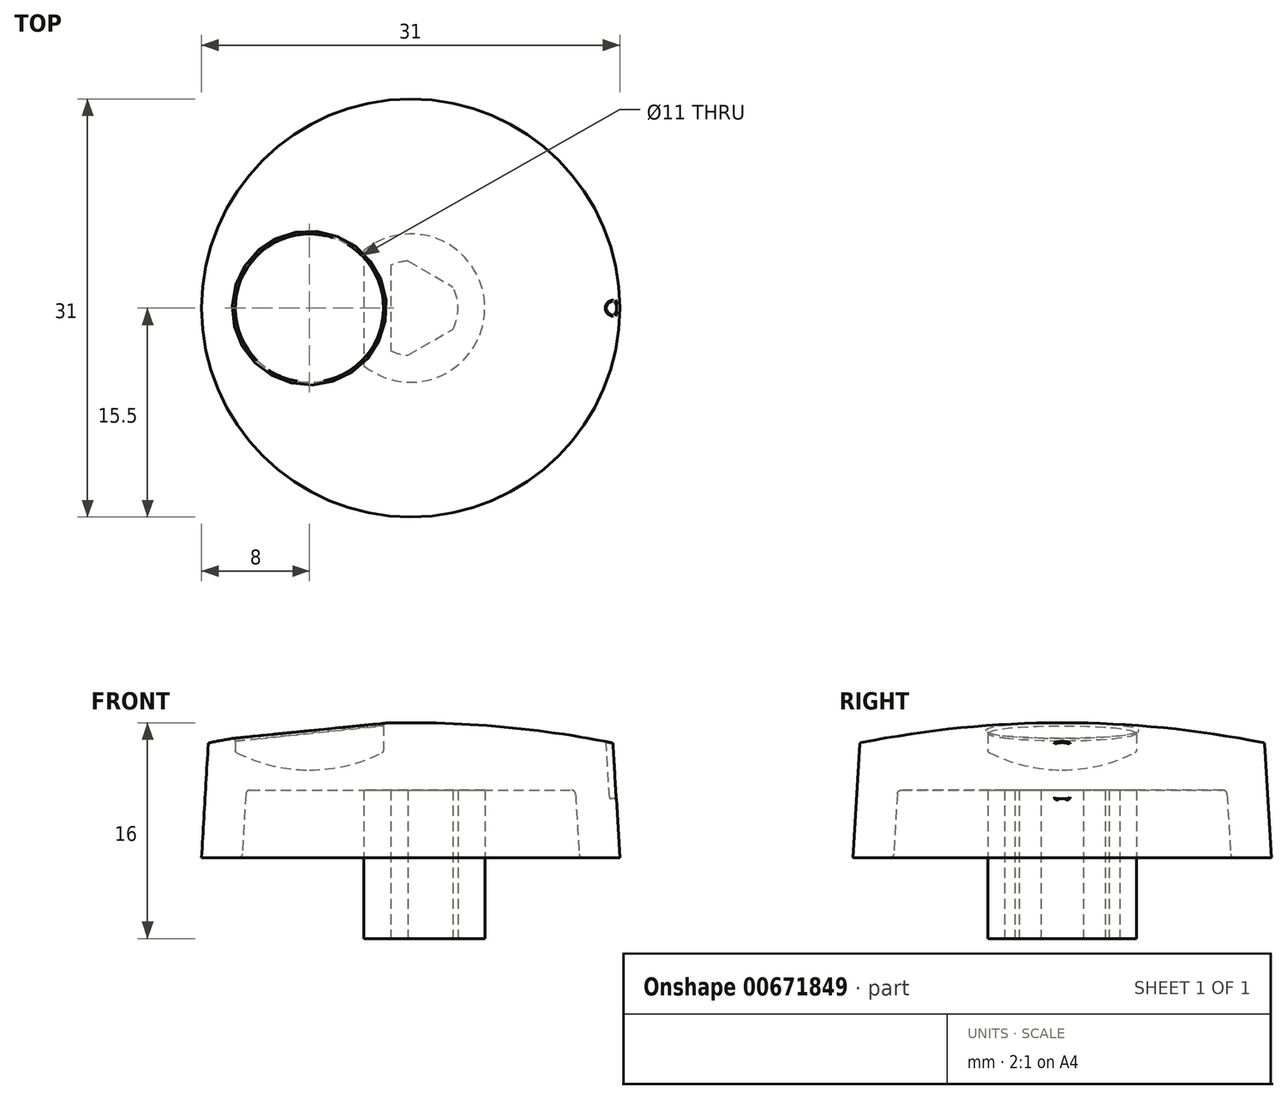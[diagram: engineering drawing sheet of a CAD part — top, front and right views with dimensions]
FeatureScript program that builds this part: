
annotation { "Feature Type Name" : "Feature", "Feature Type Description" : "" }
export const myFeature = defineFeature(function(context is Context, id is Id, definition is map)
    precondition{}
    {
        {
            assignVariable(context, id + "F0", {"name" : "height_above_panel", "anyValue" : 11});
        }
        {
            assignVariable(context, id + "F1", {"name" : "grip_depth_factor", "anyValue" : 0.75});
        }
        {
            var Q0;
            Q0=qCreatedBy(makeId("Top.planeOp"),FACE);
            var sketch = newSketch(context, id + "F2", { "sketchPlane" : qUnion([Q0])});
            skArc(sketch, "E0", {"start": v(-3.46, -4.27) * mm, "mid": v(5.5, 0) * mm, "end": v(-3.46, 4.27) * mm});
            skArc(sketch, "E1", {"start": v(-1.46, -2.62) * mm, "mid": v(3, 0.02) * mm, "end": v(-1.5, 2.6) * mm, "construction": true});
            skCircle(sketch, "E2", {"center": v(0, 0) * mm, "radius": 15.5 * mm, "construction": true});
            skLineSegment(sketch, "E3", {"start": v(-1.46, 3.18) * mm, "end": v(-1.46, -3.18) * mm});
            skLineSegment(sketch, "E4", {"start": v(-3.46, 4.27) * mm, "end": v(-3.46, -4.27) * mm});
            skArc(sketch, "E5", {"start": v(-1.46, -3.18) * mm, "mid": v(-0.85, -3.4) * mm, "end": v(-0.2, -3.5) * mm});
            skLineSegment(sketch, "E6", {"start": v(-0.2, -3.5) * mm, "end": v(3.13, -1.57) * mm});
            skArc(sketch, "E7.trimOffspring", {"start": v(3.13, -1.57) * mm, "mid": v(3.5, 0) * mm, "end": v(3.13, 1.57) * mm});
            skArc(sketch, "E8.trimOffspring", {"start": v(-0.2, 3.5) * mm, "mid": v(-0.85, 3.4) * mm, "end": v(-1.46, 3.18) * mm});
            skLineSegment(sketch, "E9.trimOffspring", {"start": v(-0.2, 3.5) * mm, "end": v(3.13, 1.57) * mm});
            skArc(sketch, "E10.0", {"start": v(-1.5, -2.51) * mm, "mid": v(2.92, -0.02) * mm, "end": v(-1.46, 2.53) * mm, "construction": true});
            skLineSegment(sketch, "E11", {"start": v(-1.5, 2.6) * mm, "end": v(-1.5, -2.51) * mm, "construction": true});
            skSolve(sketch);
        }
        {
            var Q0;
            Q0=qSketchRegion(id+"F2",true);
            extrude(context, id + "F3", {"entities" : qUnion([Q0]), "depth" : 11 * mm});
        }
        {
            var Q0;
            Q0=qCreatedBy(makeId("Top.planeOp"),FACE);
            cPlane(context, id + "F4", {"entities" : qUnion([Q0]), "cplaneType" : CPlaneType.OFFSET, "offset" : 5 * mm, "width" : 150 * mm, "height" : 150 * mm});
        }
        {
            var Q0;
            Q0=qCreatedBy(makeId("Front.planeOp"),FACE);
            var sketch = newSketch(context, id + "F5", { "sketchPlane" : qUnion([Q0])});
            skLineSegment(sketch, "E12.0", {"start": v(-3.46, 11) * mm, "end": v(5.5, 11) * mm});
            skLineSegment(sketch, "E13", {"start": v(0, 11) * mm, "end": v(0, 16) * mm});
            skArc(sketch, "E14", {"start": v(15, 14.5) * mm, "mid": v(7.54, 15.62) * mm, "end": v(0, 16) * mm});
            skLineSegment(sketch, "E15", {"start": v(-10.14, 16) * mm, "end": v(12.68, 16) * mm, "construction": true});
            skLineSegment(sketch, "E16", {"start": v(15, 14.5) * mm, "end": v(15.5, 6) * mm});
            skLineSegment(sketch, "E17", {"start": v(15.5, 6) * mm, "end": v(12.5, 6) * mm});
            skLineSegment(sketch, "E18", {"start": v(12.5, 6) * mm, "end": v(12.2, 11) * mm});
            skLineSegment(sketch, "E19", {"start": v(5.5, 11) * mm, "end": v(12.2, 11) * mm});
            skSolve(sketch);
        }
        {
            var Q0;
            {var subQ0=sQuery(id+"F5.wireOp",EDGE,"E13");Q0=makeQuery(id+"F5.imprint","IMPRINT",FACE,{"disambiguationData":[TD([[makeQuery(id+"F5.imprint","IMPRINT",EDGE,{"derivedFrom":subQ0}),-1.0]])]});}
            var Q1;
            Q1=sQuery(id+"F5.wireOp",EDGE,"E13");
            revolve(context, id + "F6", {"operationType" : NewBodyOperationType.ADD, "entities" : qUnion([Q0]), "axis" : qUnion([Q1]), "revolveType" : RevolveType.FULL});
        }
        {
            var Q0;
            Q0=qCreatedBy(makeId("Front.planeOp"),FACE);
            var sketch = newSketch(context, id + "F7", { "sketchPlane" : qUnion([Q0])});
            skLineSegment(sketch, "E20.0", {"start": v(15, 14.5) * mm, "end": v(-15, 14.5) * mm});
            skLineSegment(sketch, "E21.bottom", {"start": v(-13, 24.51) * mm, "end": v(-7.5, 24.51) * mm});
            skLineSegment(sketch, "E21.top", {"start": v(-13, 13.83) * mm, "end": v(-7.5, 13.83) * mm});
            skLineSegment(sketch, "E21.left", {"start": v(-13, 24.51) * mm, "end": v(-13, 13.83) * mm});
            skLineSegment(sketch, "E21.right", {"start": v(-7.5, 24.51) * mm, "end": v(-7.5, 13.83) * mm});
            skLineSegment(sketch, "E22", {"start": v(-15.04, 12.5) * mm, "end": v(-4.86, 12.5) * mm, "construction": true});
            skArc(sketch, "E23", {"start": v(-13, 13.83) * mm, "mid": v(-10.33, 12.84) * mm, "end": v(-7.5, 12.5) * mm});
            skLineSegment(sketch, "E24", {"start": v(-7.5, 13.83) * mm, "end": v(-7.5, 12.5) * mm});
            skSolve(sketch);
        }
        {
            var Q0;
            Q0=qSketchRegion(id+"F7",true);
            var Q1;
            Q1=sQuery(id+"F7.wireOp",EDGE,"E21.right");
            revolve(context, id + "F8", {"operationType" : NewBodyOperationType.REMOVE, "entities" : qUnion([Q0]), "axis" : qUnion([Q1]), "revolveType" : RevolveType.FULL, "oppositeDirection" : true});
        }
        {
            var Q0;
            Q0=sQuery(id+"F5.wireOp",EDGE,"E16");
            var Q1;
            Q1=sQuery(id+"F5.wireOp",VERTEX,"E16.start");
            cPlane(context, id + "F9", {"entities" : qUnion([Q0, Q1]), "cplaneType" : CPlaneType.LINE_POINT, "offset" : 25 * mm, "width" : 150 * mm, "height" : 150 * mm});
        }
        {
            var Q0;
            Q0=qCreatedBy(id+"F9.planeOp",FACE);
            var sketch = newSketch(context, id + "F10", { "sketchPlane" : qUnion([Q0])});
            skPoint(sketch, "E25.0", {"position": v(15.83, 0) * mm});
            skCircle(sketch, "E26", {"center": v(15.83, 0) * mm, "radius": 0.5 * mm});
            skSolve(sketch);
        }
        {
            var Q0;
            Q0=makeQuery(id+"F10.imprint","IMPRINT",FACE,{"disambiguationData":[TD([[makeQuery(id+"F10.imprint","IMPRINT",EDGE,{"derivedFrom":sQuery(id+"F10.wireOp",EDGE,"E26")}),1.0]])]});
            extrude(context, id + "F11", {"entities" : qUnion([Q0]), "operationType" : NewBodyOperationType.REMOVE, "endBound" : BoundingType.SYMMETRIC, "depth" : (getVariable(context, 'grip_depth_factor') * getVariable(context, 'height_above_panel')) * mm});
        }
        {
            var Q0;
            Q0=makeQuery(id+"F11.boolean.opBoolean","COPY",FACE,{"derivedFrom":makeQuery(id+"F11.opExtrude","SWEPT_FACE",FACE,{"disambiguationData":[OSD([sQuery(id+"F10.wireOp",EDGE,"E26")])]})});
            var Q1;
            Q1=makeQuery(id+"F6.opRevolve","SWEPT_EDGE",EDGE,{"disambiguationData":[OSD([sQuery(id+"F5.wireOp",EDGE,"E14"),sQuery(id+"F5.wireOp",EDGE,"E16")])]});
            fillet(context, id + "F12", {"entities" : qUnion([Q0, Q1]), "radius" : 0.1 * mm, "tangentPropagation" : true, "allowEdgeOverflow" : false});
        }
        {
            var Q0;
            Q0=makeQuery(id+"F8.boolean.opBoolean","INTERSECT",EDGE,{"derivedFrom":[makeQuery(id+"F6.opRevolve","SWEPT_FACE",FACE,{"disambiguationData":[OSD([sQuery(id+"F5.wireOp",EDGE,"E14")])]}),makeQuery(id+"F8.opRevolve","SWEPT_FACE",FACE,{"disambiguationData":[OSD([sQuery(id+"F7.wireOp",EDGE,"E21.left")])]})]});
            var Q1;
            Q1=makeQuery(id+"F8.boolean.opBoolean","COPY",EDGE,{"derivedFrom":makeQuery(id+"F8.opRevolve","SWEPT_EDGE",EDGE,{"disambiguationData":[OSD([sQuery(id+"F7.wireOp",EDGE,"E21.top"),sQuery(id+"F7.wireOp",EDGE,"E21.left"),sQuery(id+"F7.wireOp",EDGE,"E23")])]})});
            fillet(context, id + "F13", {"entities" : qUnion([Q0, Q1]), "radius" : 0.2 * mm, "tangentPropagation" : true, "allowEdgeOverflow" : false});
        }
        {
            var Q0;
            Q0=makeQuery(id+"F6.opRevolve","SWEPT_EDGE",EDGE,{"disambiguationData":[OSD([sQuery(id+"F5.wireOp",EDGE,"E18"),sQuery(id+"F5.wireOp",EDGE,"EPLxxkZY-Jm2v-z4IR-q4Ga-VjId1qaTgEh2")])]});
            var Q1;
            Q1=makeQuery(id+"F6.boolean.opBoolean","MERGE",EDGE,{"derivedFrom":[makeQuery(id+"F3.opExtrude","CAP_EDGE",EDGE,{"disambiguationData":[OSD([sQuery(id+"F2.wireOp",EDGE,"E0")])],"isStart":false}),makeQuery(id+"F6.opRevolve","SWEPT_EDGE",EDGE,{"disambiguationData":[OSD([sQuery(id+"F5.wireOp",EDGE,"E12.0"),sQuery(id+"F5.wireOp",EDGE,"EPLxxkZY-Jm2v-z4IR-q4Ga-VjId1qaTgEh2")])]})]});
            var Q2;
            Q2=makeQuery(id+"F3.opExtrude","CAP_EDGE",EDGE,{"disambiguationData":[OSD([sQuery(id+"F2.wireOp",EDGE,"E4")])],"isStart":false});
            fillet(context, id + "F14", {"entities" : qUnion([Q0, Q1, Q2]), "radius" : 0.3 * mm, "tangentPropagation" : true, "allowEdgeOverflow" : false});
        }
    });
